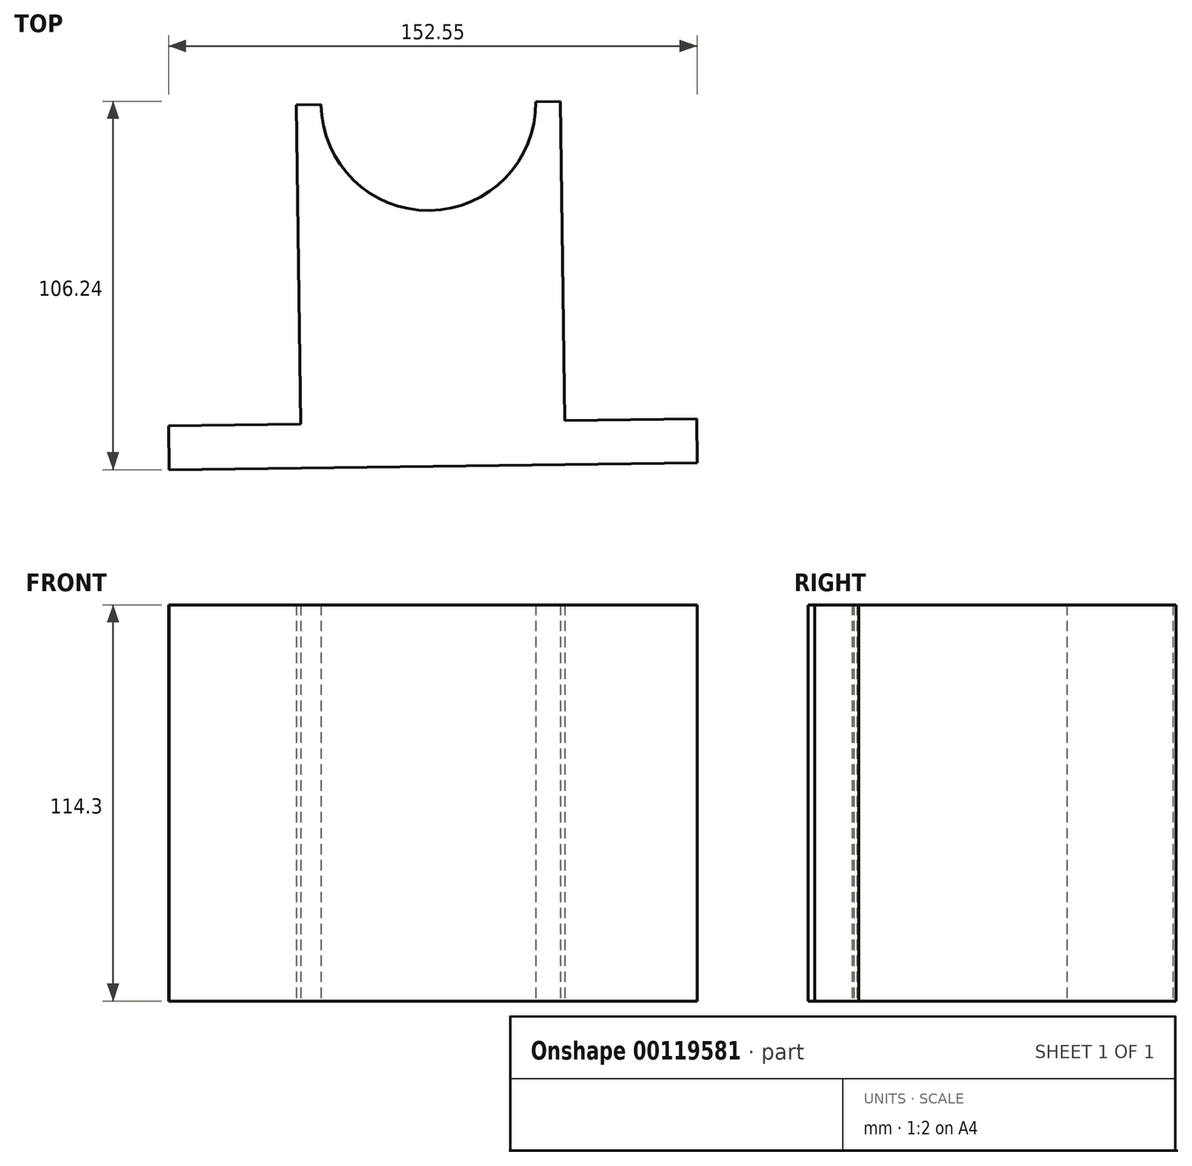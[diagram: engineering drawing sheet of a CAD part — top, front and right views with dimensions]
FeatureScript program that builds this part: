
annotation { "Feature Type Name" : "Feature", "Feature Type Description" : "" }
export const myFeature = defineFeature(function(context is Context, id is Id, definition is map)
    precondition{}
    {
        {
            var Q0;
            Q0=qCreatedBy(makeId("Top.planeOp"),FACE);
            var sketch = newSketch(context, id + "F0", { "sketchPlane" : qUnion([Q0])});
            skLineSegment(sketch, "E0", {"start": v(152.39, 1.97) * mm, "end": v(0, 0) * mm});
            skLineSegment(sketch, "E1", {"start": v(0, 0) * mm, "end": v(-0.16, 12.7) * mm});
            skLineSegment(sketch, "E2", {"start": v(-0.16, 12.7) * mm, "end": v(37.93, 13.2) * mm});
            skLineSegment(sketch, "E3", {"start": v(37.93, 13.2) * mm, "end": v(36.74, 105.26) * mm});
            skLineSegment(sketch, "E4", {"start": v(36.74, 105.26) * mm, "end": v(112.94, 106.24) * mm});
            skLineSegment(sketch, "E5", {"start": v(112.94, 106.24) * mm, "end": v(114.13, 14.18) * mm});
            skLineSegment(sketch, "E6", {"start": v(114.13, 14.18) * mm, "end": v(152.22, 14.67) * mm});
            skLineSegment(sketch, "E7", {"start": v(152.22, 14.67) * mm, "end": v(152.39, 1.97) * mm});
            skCircle(sketch, "E8", {"center": v(74.84, 105.75) * mm, "radius": 30.98 * mm});
            skSolve(sketch);
        }
        {
            var Q0;
            Q0=makeQuery(id+"F0.imprint","IMPRINT",FACE,{"disambiguationData":[TD([[makeQuery(id+"F0.imprint","IMPRINT",EDGE,{"derivedFrom":sQuery(id+"F0.wireOp",EDGE,"E0")}),-1.0]])]});
            extrude(context, id + "F1", {"entities" : qUnion([Q0]), "depth" : 114.3 * mm});
        }
    });
